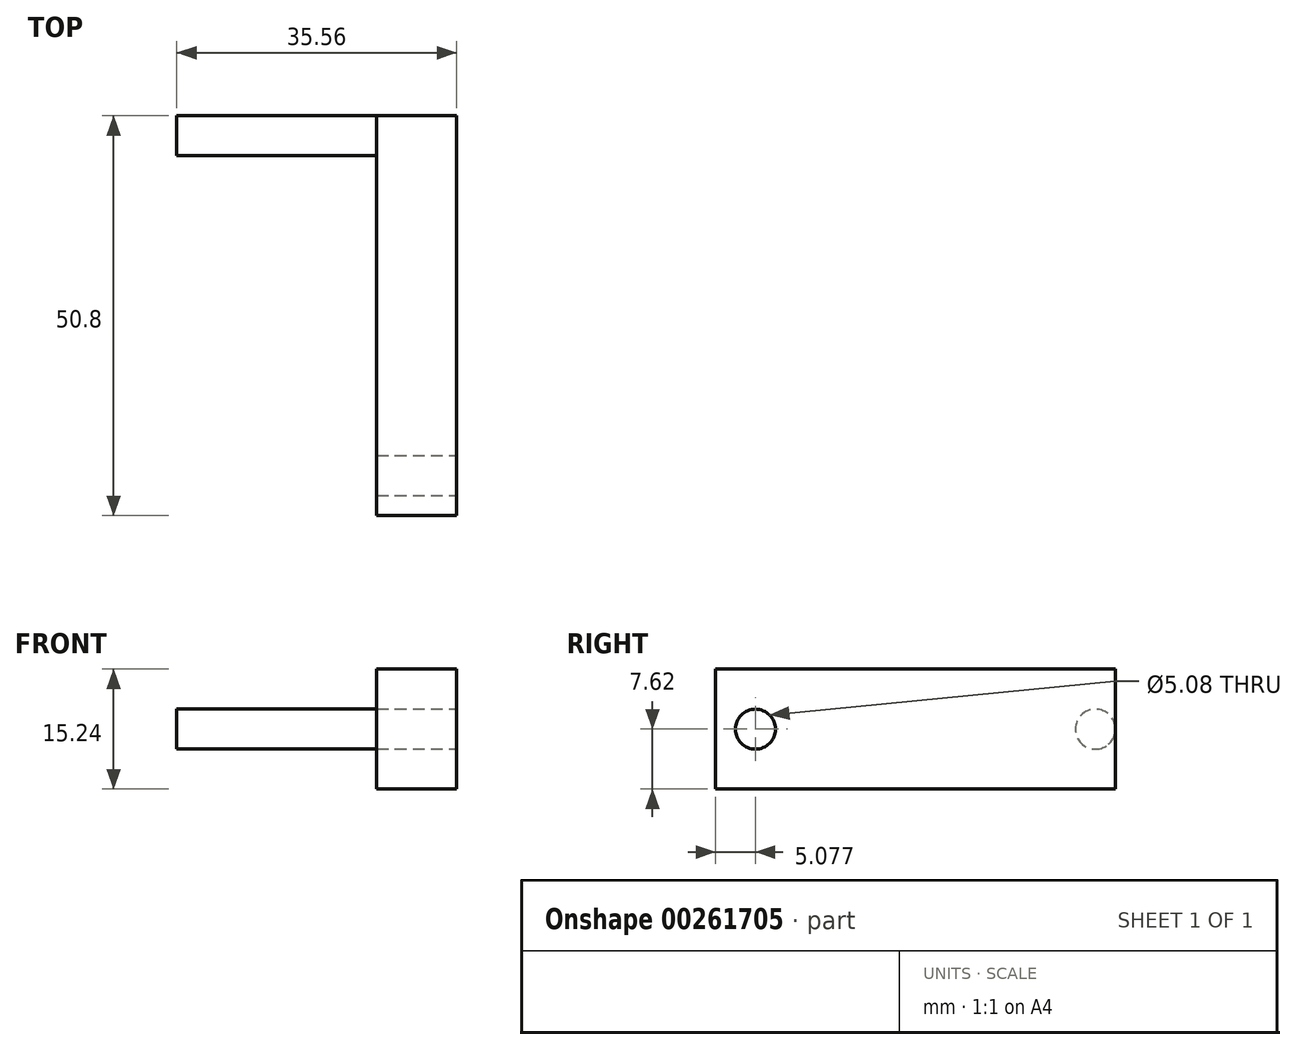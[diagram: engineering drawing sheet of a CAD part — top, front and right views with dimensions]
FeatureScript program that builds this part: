
annotation { "Feature Type Name" : "Feature", "Feature Type Description" : "" }
export const myFeature = defineFeature(function(context is Context, id is Id, definition is map)
    precondition{}
    {
        {
            var Q0;
            Q0=qCreatedBy(makeId("Right.planeOp"),FACE);
            var sketch = newSketch(context, id + "F0", { "sketchPlane" : qUnion([Q0])});
            skLineSegment(sketch, "E0.bottom", {"start": v(-21.75, 7.62) * mm, "end": v(29.05, 7.62) * mm});
            skLineSegment(sketch, "E0.top", {"start": v(-21.75, -7.62) * mm, "end": v(29.05, -7.62) * mm});
            skLineSegment(sketch, "E0.left", {"start": v(-21.75, 7.62) * mm, "end": v(-21.75, -7.62) * mm});
            skLineSegment(sketch, "E0.right", {"start": v(29.05, 7.62) * mm, "end": v(29.05, -7.62) * mm});
            skCircle(sketch, "E1", {"center": v(26.5, 0) * mm, "radius": 2.54 * mm});
            skLineSegment(sketch, "E2", {"start": v(23.97, 7.62) * mm, "end": v(23.97, -7.62) * mm});
            skCircle(sketch, "E3", {"center": v(-16.67, 0) * mm, "radius": 2.54 * mm});
            skSolve(sketch);
        }
        {
            var Q0;
            Q0=makeQuery(id+"F0.imprint","IMPRINT",FACE,{"disambiguationData":[TD([[makeQuery(id+"F0.imprint","IMPRINT",EDGE,{"derivedFrom":sQuery(id+"F0.wireOp",EDGE,"E1")}),1.0]])]});
            extrude(context, id + "F1", {"entities" : qUnion([Q0]), "oppositeDirection" : true, "depth" : 35.56 * mm});
        }
        {
            var Q0;
            {var subQ4=sQuery(id+"F0.wireOp",EDGE,"E0.left");Q0=makeQuery(id+"F0.imprint","IMPRINT",FACE,{"disambiguationData":[TD([[makeQuery(id+"F0.imprint","IMPRINT",EDGE,{"derivedFrom":subQ4}),1.0]])]});}
            var Q1;
            {var subQ0=sQuery(id+"F0.wireOp",EDGE,"E0.right");var subQ1=sQuery(id+"F0.wireOp",EDGE,"E0.top");var subQ2=makeQuery(id+"F0.imprint","INTERSECT",VERTEX,{"derivedFrom":[subQ1,subQ0]});Q1=makeQuery(id+"F0.imprint","IMPRINT",FACE,{"disambiguationData":[TD([[makeQuery(id+"F0.imprint","IMPRINT",EDGE,{"disambiguationData":[TD([[subQ2,1.0]])],"derivedFrom":subQ1}),1.0]])]});}
            extrude(context, id + "F2", {"entities" : qUnion([Q0, Q1]), "operationType" : NewBodyOperationType.ADD, "oppositeDirection" : true, "depth" : 10.16 * mm});
        }
        {
            var Q0;
            {var subQ0=sQuery(id+"F0.wireOp",EDGE,"E0.right");var subQ1=sQuery(id+"F0.wireOp",EDGE,"E0.bottom");var subQ2=makeQuery(id+"F0.imprint","INTERSECT",VERTEX,{"derivedFrom":[subQ1,subQ0]});Q0=makeQuery(id+"F0.imprint","IMPRINT",FACE,{"disambiguationData":[TD([[makeQuery(id+"F0.imprint","IMPRINT",EDGE,{"disambiguationData":[TD([[subQ2,1.0]])],"derivedFrom":subQ1}),-1.0]])]});}
            extrude(context, id + "F3", {"entities" : qUnion([Q0]), "operationType" : NewBodyOperationType.ADD, "oppositeDirection" : true, "depth" : 10.16 * mm});
        }
    });
